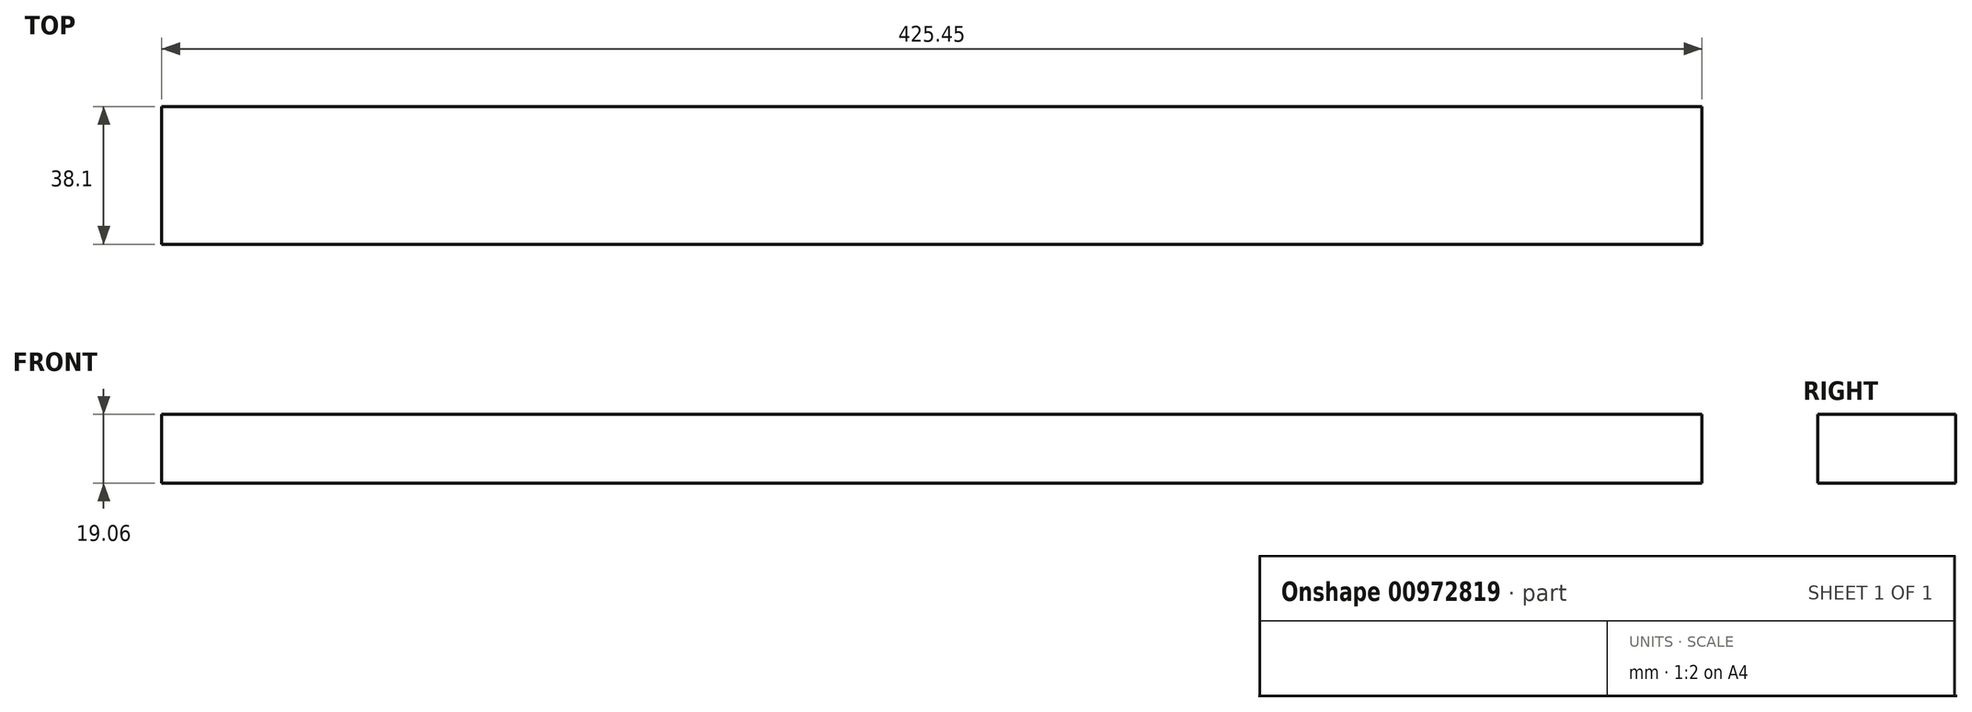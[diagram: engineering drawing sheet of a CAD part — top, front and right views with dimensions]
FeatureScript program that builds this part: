
annotation { "Feature Type Name" : "Feature", "Feature Type Description" : "" }
export const myFeature = defineFeature(function(context is Context, id is Id, definition is map)
    precondition{}
    {
        {
            var Q0;
            Q0=qCreatedBy(makeId("Right.planeOp"),FACE);
            var sketch = newSketch(context, id + "F0", { "sketchPlane" : qUnion([Q0])});
            skLineSegment(sketch, "E0.bottom", {"start": v(19.05, 9.53) * mm, "end": v(-19.05, 9.53) * mm});
            skLineSegment(sketch, "E0.top", {"start": v(19.05, -9.53) * mm, "end": v(-19.05, -9.53) * mm});
            skLineSegment(sketch, "E0.left", {"start": v(19.05, 9.53) * mm, "end": v(19.05, -9.53) * mm});
            skLineSegment(sketch, "E0.right", {"start": v(-19.05, 9.53) * mm, "end": v(-19.05, -9.53) * mm});
            skPoint(sketch, "E0.middle", {"position": v(0, 0) * mm});
            skSolve(sketch);
        }
        {
            var Q0;
            Q0=makeQuery(id+"F0.imprint","IMPRINT",FACE,{"disambiguationData":[TD([[makeQuery(id+"F0.imprint","IMPRINT",EDGE,{"derivedFrom":sQuery(id+"F0.wireOp",EDGE,"E0.bottom")}),1.0]])]});
            extrude(context, id + "F1", {"entities" : qUnion([Q0]), "depth" : 425.45 * mm, "offsetDistance" : 25.4 * mm});
        }
    });
